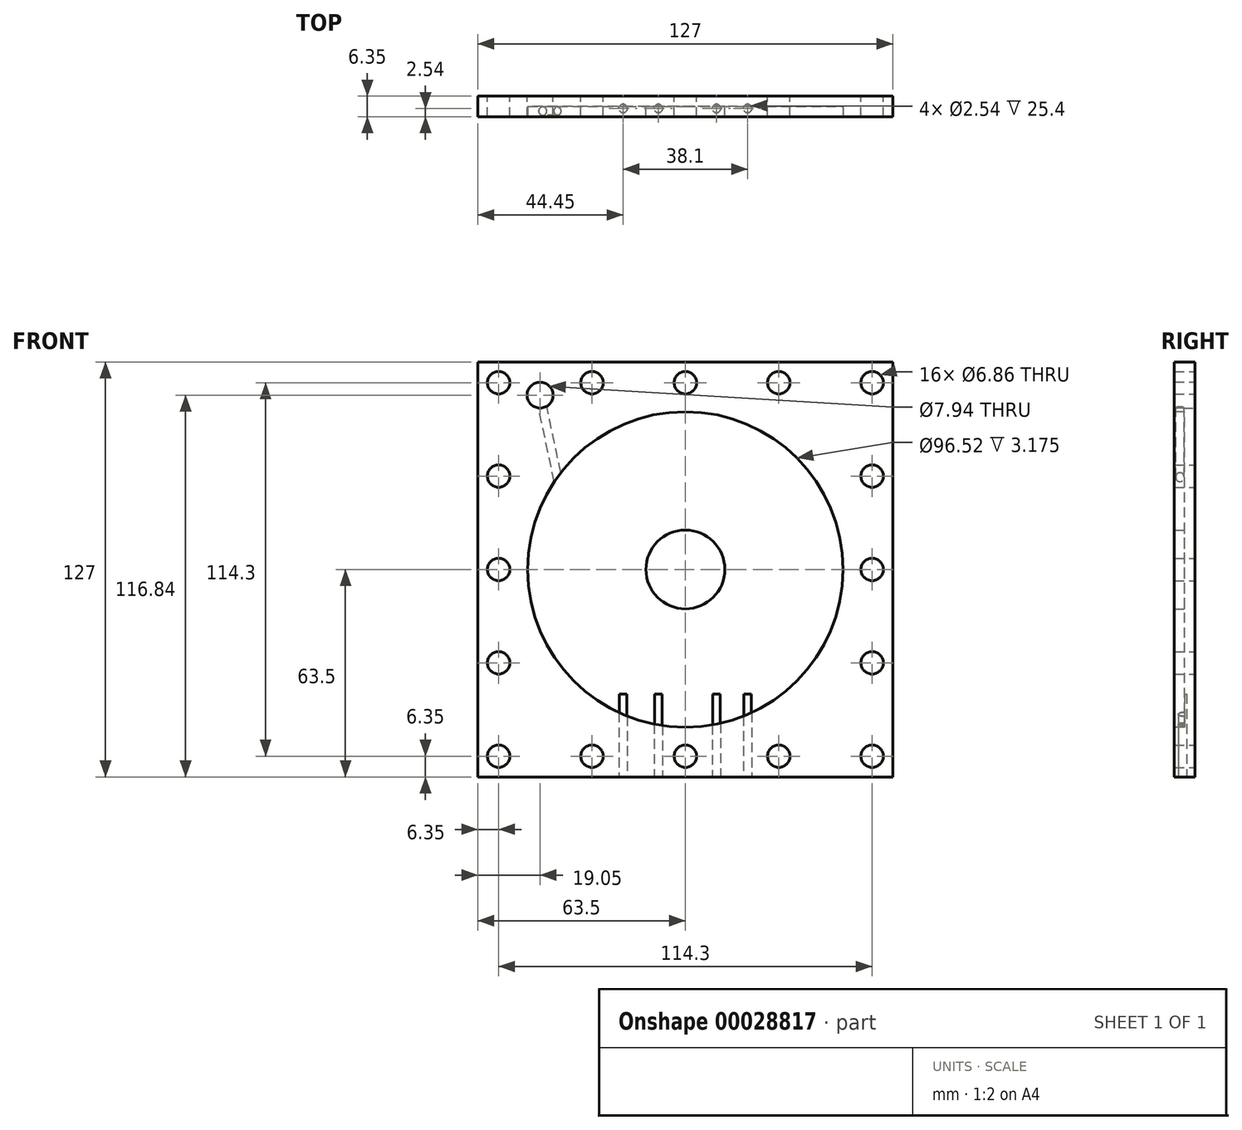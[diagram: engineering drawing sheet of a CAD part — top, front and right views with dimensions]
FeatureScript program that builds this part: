
annotation { "Feature Type Name" : "Feature", "Feature Type Description" : "" }
export const myFeature = defineFeature(function(context is Context, id is Id, definition is map)
    precondition{}
    {
        {
            var Q0;
            Q0=qCreatedBy(makeId("Front.planeOp"),FACE);
            var sketch = newSketch(context, id + "F0", { "sketchPlane" : qUnion([Q0])});
            skLineSegment(sketch, "E0.rect.bottom", {"start": v(63.5, 63.5) * mm, "end": v(-63.5, 63.5) * mm});
            skLineSegment(sketch, "E0.rect.top", {"start": v(63.5, -63.5) * mm, "end": v(-63.5, -63.5) * mm});
            skLineSegment(sketch, "E0.rect.left", {"start": v(63.5, 63.5) * mm, "end": v(63.5, -63.5) * mm});
            skLineSegment(sketch, "E0.rect.right", {"start": v(-63.5, 63.5) * mm, "end": v(-63.5, -63.5) * mm});
            skPoint(sketch, "E0.rect.middle", {"position": v(0, 0) * mm});
            skCircle(sketch, "E1", {"center": v(-44.45, 53.34) * mm, "radius": 3.97 * mm});
            skCircle(sketch, "E2", {"center": v(0, 0) * mm, "radius": 47.56 * mm, "construction": true});
            skLineSegment(sketch, "E3.rect.bottom", {"start": v(-57.15, 57.15) * mm, "end": v(57.15, 57.15) * mm, "construction": true});
            skLineSegment(sketch, "E3.rect.top", {"start": v(-57.15, -57.15) * mm, "end": v(57.15, -57.15) * mm, "construction": true});
            skLineSegment(sketch, "E3.rect.left", {"start": v(-57.15, 57.15) * mm, "end": v(-57.15, -57.15) * mm, "construction": true});
            skLineSegment(sketch, "E3.rect.right", {"start": v(57.15, 57.15) * mm, "end": v(57.15, -57.15) * mm, "construction": true});
            skPoint(sketch, "E4", {"position": v(0, 57.15) * mm});
            skPoint(sketch, "E5", {"position": v(57.15, 0) * mm});
            skPoint(sketch, "E6", {"position": v(0, -57.15) * mm});
            skPoint(sketch, "E7", {"position": v(-57.15, 0) * mm});
            skCircle(sketch, "E8", {"center": v(-57.15, 57.15) * mm, "radius": 3.43 * mm});
            skCircle(sketch, "E9", {"center": v(0, 57.15) * mm, "radius": 3.43 * mm});
            skCircle(sketch, "E10", {"center": v(57.15, 57.15) * mm, "radius": 3.43 * mm});
            skCircle(sketch, "E11", {"center": v(57.15, 0) * mm, "radius": 3.43 * mm});
            skCircle(sketch, "E12", {"center": v(57.15, -57.15) * mm, "radius": 3.43 * mm});
            skCircle(sketch, "E13", {"center": v(0, -57.15) * mm, "radius": 3.43 * mm});
            skCircle(sketch, "E14", {"center": v(-57.15, -57.15) * mm, "radius": 3.43 * mm});
            skCircle(sketch, "E15", {"center": v(-57.15, 0) * mm, "radius": 3.43 * mm});
            skLineSegment(sketch, "E16.rect.bottom", {"start": v(-50, 50) * mm, "end": v(50, 50) * mm, "construction": true});
            skLineSegment(sketch, "E16.rect.top", {"start": v(-50, -50) * mm, "end": v(50, -50) * mm, "construction": true});
            skLineSegment(sketch, "E16.rect.left", {"start": v(-50, 50) * mm, "end": v(-50, -50) * mm, "construction": true});
            skLineSegment(sketch, "E16.rect.right", {"start": v(50, 50) * mm, "end": v(50, -50) * mm, "construction": true});
            skCircle(sketch, "E17", {"center": v(28.57, 57.15) * mm, "radius": 3.43 * mm});
            skCircle(sketch, "E18", {"center": v(57.15, 28.58) * mm, "radius": 3.43 * mm});
            skCircle(sketch, "E19", {"center": v(57.15, -28.58) * mm, "radius": 3.43 * mm});
            skCircle(sketch, "E20", {"center": v(28.58, -57.15) * mm, "radius": 3.43 * mm});
            skCircle(sketch, "E21", {"center": v(-28.58, -57.15) * mm, "radius": 3.43 * mm});
            skCircle(sketch, "E22", {"center": v(-57.15, -28.58) * mm, "radius": 3.43 * mm});
            skCircle(sketch, "E23", {"center": v(-57.15, 28.58) * mm, "radius": 3.43 * mm});
            skCircle(sketch, "E24", {"center": v(-28.58, 57.15) * mm, "radius": 3.43 * mm});
            skSolve(sketch);
        }
        {
            var Q0;
            Q0=qSketchRegion(id+"F0",true);
            var Q1;
            {var subQ21=sQuery(id+"F0.wireOp",EDGE,"f6949425-b88c-4a0e-8302-07c829dae053.0");var subQ27=sQuery(id+"F0.wireOp",EDGE,"5bd9be1d-ee3e-4944-9718-c5885c81100e");var subQ29=makeQuery(id+"F0.imprint","INTERSECT",VERTEX,{"derivedFrom":[subQ21,subQ27]});Q1=makeQuery(id+"F0.imprint","IMPRINT",FACE,{"disambiguationData":[TD([[makeQuery(id+"F0.imprint","IMPRINT",EDGE,{"disambiguationData":[TD([[subQ29,-1.0]])],"derivedFrom":subQ21}),-1.0]])]});}
            extrude(context, id + "F1", {"entities" : qUnion([Q0, Q1]), "depth" : 6.35 * mm});
        }
        {
            var Q0;
            Q0=makeQuery(id+"F1.opExtrude","CAP_FACE",FACE,{"disambiguationData":[OSD([sQuery(id+"F0.wireOp",EDGE,"E0.rect.bottom"),sQuery(id+"F0.wireOp",EDGE,"E0.rect.top"),sQuery(id+"F0.wireOp",EDGE,"E0.rect.left"),sQuery(id+"F0.wireOp",EDGE,"E0.rect.right"),sQuery(id+"F0.wireOp",EDGE,"1b772a9f-1761-4584-9b2b-9508be88e127"),sQuery(id+"F0.wireOp",EDGE,"5bd9be1d-ee3e-4944-9718-c5885c81100e"),sQuery(id+"F0.wireOp",EDGE,"a4b3396b-acb1-4126-9ecc-f22d3d9e1673"),sQuery(id+"F0.wireOp",EDGE,"6f9071d3-dfce-459a-96f3-6cfad81b1998"),sQuery(id+"F0.wireOp",EDGE,"8e253895-448c-4740-8d73-7ad6095a0958"),sQuery(id+"F0.wireOp",EDGE,"49ddc21f-956a-45ed-accb-e36c5fb570fd"),sQuery(id+"F0.wireOp",EDGE,"4c855955-bd80-4a33-8133-648448e085db"),sQuery(id+"F0.wireOp",EDGE,"5388e59b-5754-40e4-abb9-c8fe2573278b"),sQuery(id+"F0.wireOp",EDGE,"cb97a597-6742-4d9a-a243-e93a22987a54"),sQuery(id+"F0.wireOp",EDGE,"2f3ac294-263d-4671-b671-df59b6b99c8d")])],"isStart":false});
            var sketch = newSketch(context, id + "F2", { "sketchPlane" : qUnion([Q0])});
            skCircle(sketch, "E25", {"center": v(0, 0) * mm, "radius": 48.26 * mm});
            skSolve(sketch);
        }
        {
            var Q0;
            Q0=qSketchRegion(id+"F2",true);
            extrude(context, id + "F3", {"entities" : qUnion([Q0]), "operationType" : NewBodyOperationType.REMOVE, "oppositeDirection" : true, "depth" : 3.17 * mm});
        }
        {
            var Q0;
            Q0=makeQuery(id+"F3.boolean.opBoolean","COPY",FACE,{"derivedFrom":makeQuery(id+"F3.opExtrude","CAP_FACE",FACE,{"disambiguationData":[OSD([sQuery(id+"F2.wireOp",EDGE,"E25")])],"isStart":false})});
            var sketch = newSketch(context, id + "F4", { "sketchPlane" : qUnion([Q0])});
            skCircle(sketch, "E26", {"center": v(0, 0) * mm, "radius": 12.07 * mm});
            skSolve(sketch);
        }
        {
            var Q0;
            Q0=qSketchRegion(id+"F4",true);
            extrude(context, id + "F5", {"entities" : qUnion([Q0]), "operationType" : NewBodyOperationType.ADD, "depth" : 3.17 * mm});
        }
        {
            var Q0;
            Q0=makeQuery(id+"F1.opExtrude","CAP_FACE",FACE,{"disambiguationData":[OSD([sQuery(id+"F0.wireOp",EDGE,"E0.rect.bottom"),sQuery(id+"F0.wireOp",EDGE,"E0.rect.top"),sQuery(id+"F0.wireOp",EDGE,"E0.rect.left"),sQuery(id+"F0.wireOp",EDGE,"E0.rect.right"),sQuery(id+"F0.wireOp",EDGE,"E1"),sQuery(id+"F0.wireOp",EDGE,"E8"),sQuery(id+"F0.wireOp",EDGE,"E9"),sQuery(id+"F0.wireOp",EDGE,"E10"),sQuery(id+"F0.wireOp",EDGE,"E11"),sQuery(id+"F0.wireOp",EDGE,"E12"),sQuery(id+"F0.wireOp",EDGE,"E13"),sQuery(id+"F0.wireOp",EDGE,"E14"),sQuery(id+"F0.wireOp",EDGE,"E15")])],"isStart":false});
            var sketch = newSketch(context, id + "F6", { "sketchPlane" : qUnion([Q0])});
            skLineSegment(sketch, "E27", {"start": v(-44.45, 53.34) * mm, "end": v(-94.91, 42.61) * mm, "construction": true});
            skSolve(sketch);
        }
        {
            var Q0;
            Q0=sQuery(id+"F6.wireOp",EDGE,"E27");
            cPlane(context, id + "F7", {"entities" : qUnion([Q0]), "cplaneType" : CPlaneType.LINE_ANGLE, "offset" : 152.4 * mm, "angle" : 90 * degree, "width" : 152.4 * mm, "height" : 152.4 * mm});
        }
        {
            var Q0;
            Q0=qCreatedBy(id+"F7.planeOp",FACE);
            var sketch = newSketch(context, id + "F8", { "sketchPlane" : qUnion([Q0])});
            skCircle(sketch, "E28", {"center": v(-32.39, -4.6) * mm, "radius": 1.27 * mm});
            skLineSegment(sketch, "E29", {"start": v(-32.39, -4.6) * mm, "end": v(-32.39, -6.35) * mm, "construction": true});
            skSolve(sketch);
        }
        {
            var Q0;
            Q0=qSketchRegion(id+"F8",true);
            var Q1;
            Q1=makeQuery(id+"F3.boolean.opBoolean","COPY",FACE,{"derivedFrom":makeQuery(id+"F3.opExtrude","SWEPT_FACE",FACE,{"disambiguationData":[OSD([sQuery(id+"F2.wireOp",EDGE,"E25")])]})});
            extrude(context, id + "F9", {"entities" : qUnion([Q0]), "operationType" : NewBodyOperationType.REMOVE, "endBound" : BoundingType.UP_TO_SURFACE, "oppositeDirection" : true, "endBoundEntityFace" : qUnion([Q1]), "depth" : 25.4 * mm});
        }
        {
            var Q0;
            Q0=makeQuery(id+"F1.opExtrude","SWEPT_FACE",FACE,{"disambiguationData":[OSD([sQuery(id+"F0.wireOp",EDGE,"E0.rect.top")])]});
            var sketch = newSketch(context, id + "F10", { "sketchPlane" : qUnion([Q0])});
            skCircle(sketch, "E30", {"center": v(-19.05, 3.81) * mm, "radius": 1.27 * mm});
            skCircle(sketch, "E31", {"center": v(-8.25, 3.81) * mm, "radius": 1.27 * mm});
            skCircle(sketch, "E32", {"center": v(9.53, 3.81) * mm, "radius": 1.27 * mm});
            skCircle(sketch, "E33", {"center": v(19.05, 3.81) * mm, "radius": 1.27 * mm});
            skSolve(sketch);
        }
        {
            var Q0;
            Q0=qSketchRegion(id+"F10",true);
            extrude(context, id + "F11", {"entities" : qUnion([Q0]), "operationType" : NewBodyOperationType.REMOVE, "oppositeDirection" : true, "depth" : 25.4 * mm});
        }
    });
